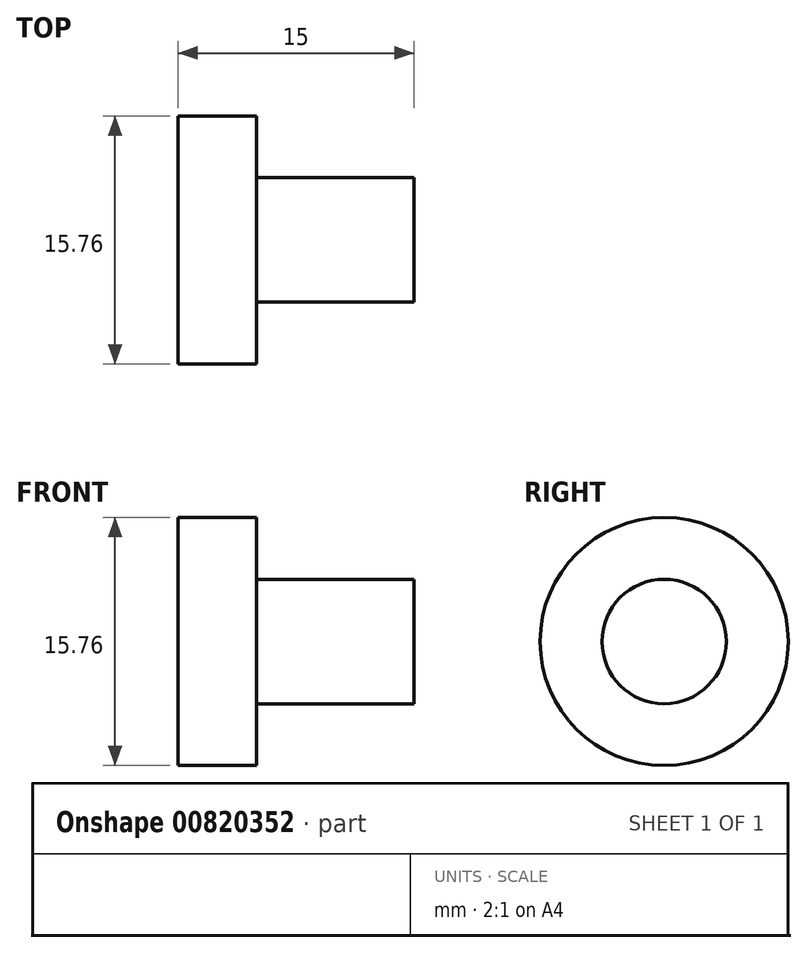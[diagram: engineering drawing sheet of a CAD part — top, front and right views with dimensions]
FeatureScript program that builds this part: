
annotation { "Feature Type Name" : "Feature", "Feature Type Description" : "" }
export const myFeature = defineFeature(function(context is Context, id is Id, definition is map)
    precondition{}
    {
        {
            var Q0;
            Q0=qCreatedBy(makeId("Front.planeOp"),FACE);
            var sketch = newSketch(context, id + "F0", { "sketchPlane" : qUnion([Q0])});
            skLineSegment(sketch, "E0", {"start": v(0, 0) * mm, "end": v(0, 7.88) * mm});
            skLineSegment(sketch, "E1", {"start": v(0, 7.88) * mm, "end": v(5, 7.88) * mm});
            skLineSegment(sketch, "E2", {"start": v(5, 7.88) * mm, "end": v(5, 3.95) * mm});
            skLineSegment(sketch, "E3", {"start": v(5, 3.95) * mm, "end": v(15, 3.95) * mm});
            skLineSegment(sketch, "E4", {"start": v(15, 3.95) * mm, "end": v(15, 0) * mm});
            skLineSegment(sketch, "E5", {"start": v(15, 0) * mm, "end": v(0, 0) * mm});
            skSolve(sketch);
        }
        {
            var Q0;
            Q0=makeQuery(id+"F0.imprint","IMPRINT",FACE,{"disambiguationData":[TD([[makeQuery(id+"F0.imprint","IMPRINT",EDGE,{"derivedFrom":sQuery(id+"F0.wireOp",EDGE,"E0")}),-1.0]])]});
            var Q1;
            Q1=sQuery(id+"F0.wireOp",EDGE,"E5");
            revolve(context, id + "F1", {"surfaceOperationType" : NewSurfaceOperationType.NEW, "entities" : qUnion([Q0]), "axis" : qUnion([Q1]), "revolveType" : RevolveType.FULL});
        }
    });
